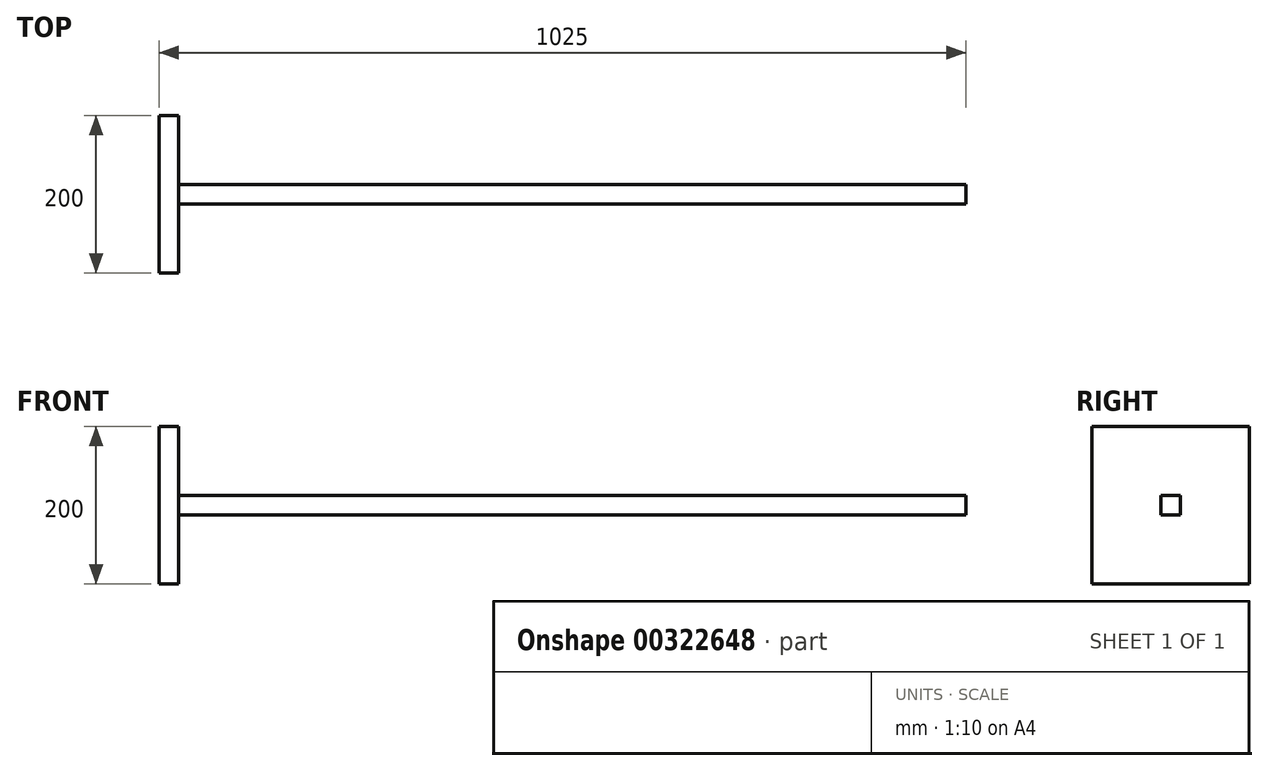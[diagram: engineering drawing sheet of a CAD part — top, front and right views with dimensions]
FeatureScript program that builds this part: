
annotation { "Feature Type Name" : "Feature", "Feature Type Description" : "" }
export const myFeature = defineFeature(function(context is Context, id is Id, definition is map)
    precondition{}
    {
        {
            var Q0;
            Q0=qCreatedBy(makeId("Right.planeOp"),FACE);
            var sketch = newSketch(context, id + "F0", { "sketchPlane" : qUnion([Q0])});
            skLineSegment(sketch, "E0.bottom", {"start": v(12.5, -12.5) * mm, "end": v(-12.5, -12.5) * mm});
            skLineSegment(sketch, "E0.top", {"start": v(12.5, 12.5) * mm, "end": v(-12.5, 12.5) * mm});
            skLineSegment(sketch, "E0.left", {"start": v(12.5, -12.5) * mm, "end": v(12.5, 12.5) * mm});
            skLineSegment(sketch, "E0.right", {"start": v(-12.5, -12.5) * mm, "end": v(-12.5, 12.5) * mm});
            skPoint(sketch, "E0.middle", {"position": v(0, 0) * mm});
            skSolve(sketch);
        }
        {
            var Q0;
            Q0=makeQuery(id+"F0.imprint","IMPRINT",FACE,{"disambiguationData":[TD([[makeQuery(id+"F0.imprint","IMPRINT",EDGE,{"derivedFrom":sQuery(id+"F0.wireOp",EDGE,"E0.bottom")}),-1.0]])]});
            extrude(context, id + "F1", {"entities" : qUnion([Q0]), "depth" : 1000 * mm});
        }
        {
            var Q0;
            Q0=makeQuery(id+"F1.opExtrude","CAP_FACE",FACE,{"disambiguationData":[OSD([sQuery(id+"F0.wireOp",EDGE,"E0.bottom"),sQuery(id+"F0.wireOp",EDGE,"E0.top"),sQuery(id+"F0.wireOp",EDGE,"E0.left"),sQuery(id+"F0.wireOp",EDGE,"E0.right")])],"isStart":true});
            var sketch = newSketch(context, id + "F2", { "sketchPlane" : qUnion([Q0])});
            skLineSegment(sketch, "E1.bottom", {"start": v(100, -100) * mm, "end": v(-100, -100) * mm});
            skLineSegment(sketch, "E1.top", {"start": v(100, 100) * mm, "end": v(-100, 100) * mm});
            skLineSegment(sketch, "E1.left", {"start": v(100, -100) * mm, "end": v(100, 100) * mm});
            skLineSegment(sketch, "E1.right", {"start": v(-100, -100) * mm, "end": v(-100, 100) * mm});
            skPoint(sketch, "E1.middle", {"position": v(0, 0) * mm});
            skSolve(sketch);
        }
        {
            var Q0;
            Q0=makeQuery(id+"F2.imprint","IMPRINT",FACE,{"disambiguationData":[TD([[makeQuery(id+"F2.imprint","IMPRINT",EDGE,{"derivedFrom":sQuery(id+"F2.wireOp",EDGE,"E1.bottom")}),-1.0]])]});
            var Q1;
            Q1=makeQuery(id+"F2.imprint","IMPRINT",FACE,{"disambiguationData":[TD([[makeQuery(id+"F2.imprint","IMPRINT",EDGE,{"derivedFrom":makeQuery(id+"F1.opExtrude","CAP_EDGE",EDGE,{"disambiguationData":[OSD([sQuery(id+"F0.wireOp",EDGE,"E0.bottom")])],"isStart":true})}),1.0]])]});
            extrude(context, id + "F3", {"entities" : qUnion([Q0, Q1]), "depth" : 25 * mm});
        }
    });
